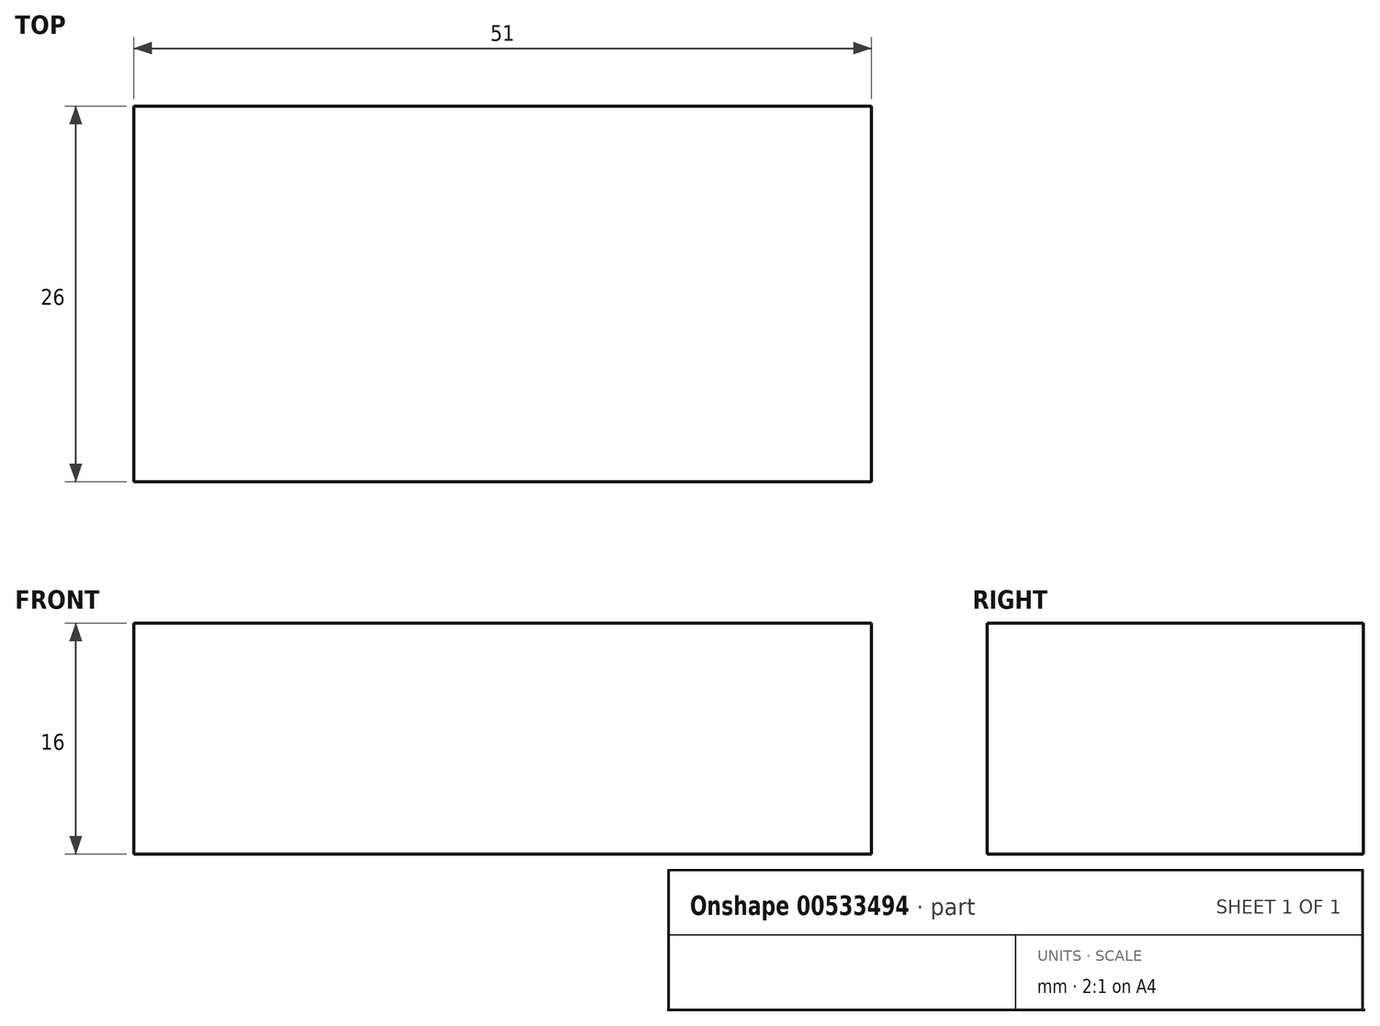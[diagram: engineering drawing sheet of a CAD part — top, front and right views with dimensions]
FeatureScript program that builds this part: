
annotation { "Feature Type Name" : "Feature", "Feature Type Description" : "" }
export const myFeature = defineFeature(function(context is Context, id is Id, definition is map)
    precondition{}
    {
        {
            var Q0;
            Q0=qCreatedBy(makeId("Top.planeOp"),FACE);
            var sketch = newSketch(context, id + "F0", { "sketchPlane" : qUnion([Q0])});
            skLineSegment(sketch, "E0.bottom", {"start": v(0, 0) * mm, "end": v(51, 0) * mm});
            skLineSegment(sketch, "E0.top", {"start": v(0, 26) * mm, "end": v(51, 26) * mm});
            skLineSegment(sketch, "E0.left", {"start": v(0, 0) * mm, "end": v(0, 26) * mm});
            skLineSegment(sketch, "E0.right", {"start": v(51, 0) * mm, "end": v(51, 26) * mm});
            skSolve(sketch);
        }
        {
            var Q0;
            Q0 = qSketchRegion(id + "F0", true);
            extrude(context, id + "F1", {"entities" : qUnion([Q0]), "depth" : 16 * mm, "offsetDistance" : 25 * mm});
        }
    });
